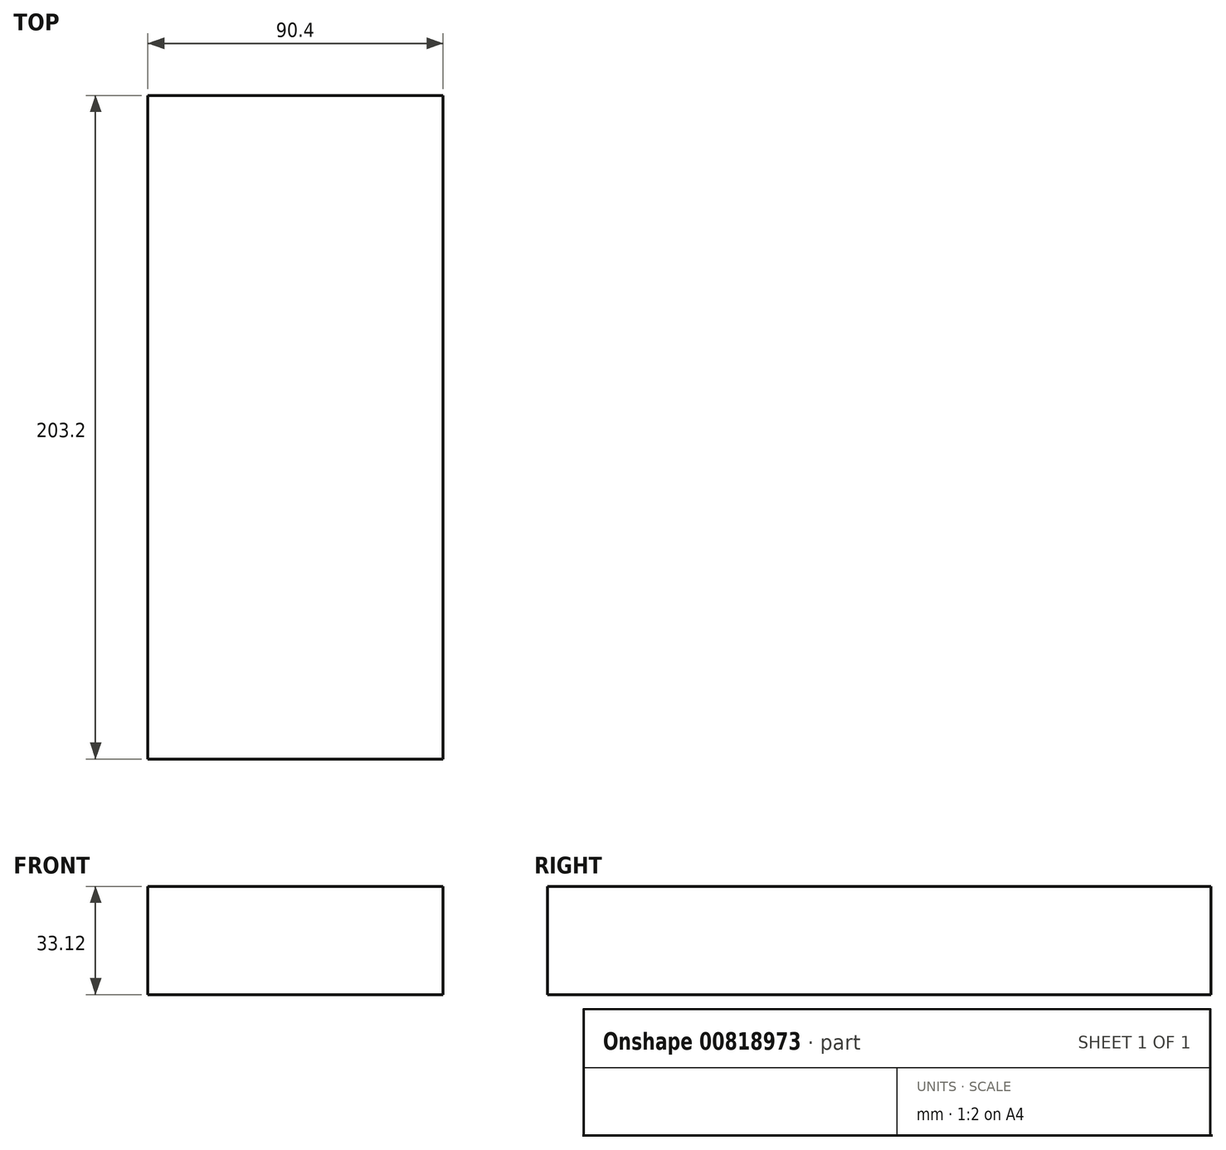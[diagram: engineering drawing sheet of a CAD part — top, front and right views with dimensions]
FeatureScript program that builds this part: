
annotation { "Feature Type Name" : "Feature", "Feature Type Description" : "" }
export const myFeature = defineFeature(function(context is Context, id is Id, definition is map)
    precondition{}
    {
        {
            var Q0;
            Q0=qCreatedBy(makeId("Front.planeOp"),FACE);
            var sketch = newSketch(context, id + "F0", { "sketchPlane" : qUnion([Q0])});
            skLineSegment(sketch, "E0.bottom", {"start": v(-45.2, 18.73) * mm, "end": v(45.2, 18.73) * mm});
            skLineSegment(sketch, "E0.top", {"start": v(-45.2, -14.39) * mm, "end": v(45.2, -14.39) * mm});
            skLineSegment(sketch, "E0.left", {"start": v(-45.2, 18.73) * mm, "end": v(-45.2, -14.39) * mm});
            skLineSegment(sketch, "E0.right", {"start": v(45.2, 18.73) * mm, "end": v(45.2, -14.39) * mm});
            skPoint(sketch, "E0.middle", {"position": v(0, 2.17) * mm});
            skSolve(sketch);
        }
        {
            var Q0;
            Q0 = qSketchRegion(id + "F0", true);
            extrude(context, id + "F1", {"entities" : qUnion([Q0]), "depth" : 25.4 * mm, "offsetDistance" : 25.4 * mm});
        }
        {
            var Q0;
            Q0=makeQuery(id+"F1.opExtrude","CAP_FACE",FACE,{"disambiguationData":[OSD([sQuery(id+"F0.wireOp",EDGE,"E0.bottom"),sQuery(id+"F0.wireOp",EDGE,"E0.top"),sQuery(id+"F0.wireOp",EDGE,"E0.left"),sQuery(id+"F0.wireOp",EDGE,"E0.right")])],"isStart":false});
            extrude(context, id + "F2", {"entities" : qUnion([Q0]), "operationType" : NewBodyOperationType.ADD, "depth" : 177.8 * mm, "offsetDistance" : 25.4 * mm});
        }
    });
